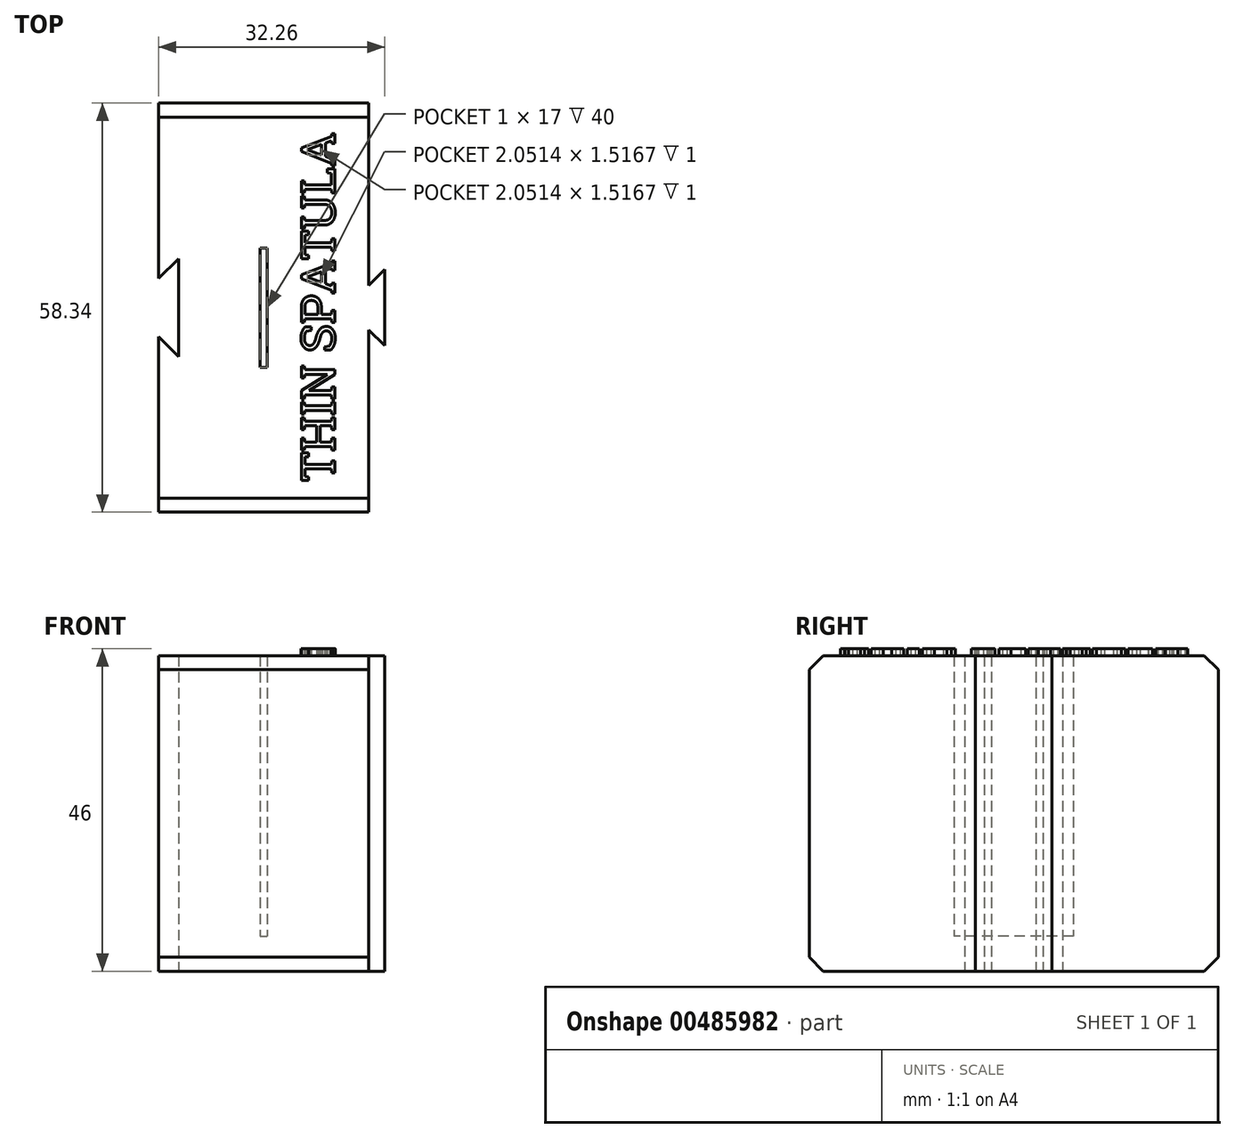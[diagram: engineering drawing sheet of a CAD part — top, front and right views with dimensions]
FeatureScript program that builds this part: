
annotation { "Feature Type Name" : "Feature", "Feature Type Description" : "" }
export const myFeature = defineFeature(function(context is Context, id is Id, definition is map)
    precondition{}
    {
        {
            var Q0;
            Q0=qCreatedBy(makeId("Top.planeOp"),FACE);
            var sketch = newSketch(context, id + "F0", { "sketchPlane" : qUnion([Q0])});
            skLineSegment(sketch, "E0", {"start": v(-15, 4.17) * mm, "end": v(-15, 29.17) * mm});
            skLineSegment(sketch, "E1", {"start": v(-15, 29.17) * mm, "end": v(15, 29.17) * mm});
            skLineSegment(sketch, "E2", {"start": v(15, 29.17) * mm, "end": v(15, 3.17) * mm});
            skLineSegment(sketch, "E3", {"start": v(-15, 4.17) * mm, "end": v(-12.17, 7) * mm});
            skLineSegment(sketch, "E4", {"start": v(-12.17, 7) * mm, "end": v(-12.17, 0) * mm});
            skLineSegment(sketch, "E5", {"start": v(15, 3.17) * mm, "end": v(17.26, 5.43) * mm});
            skLineSegment(sketch, "E6", {"start": v(17.26, 5.43) * mm, "end": v(17.26, -0.57) * mm});
            skLineSegment(sketch, "E7.MirrorCS", {"start": v(-15, -4.17) * mm, "end": v(-12.17, -7) * mm});
            skLineSegment(sketch, "E8.MirrorCS", {"start": v(15, -29.17) * mm, "end": v(15, -3.17) * mm});
            skLineSegment(sketch, "E9.MirrorCS", {"start": v(-12.17, -7) * mm, "end": v(-12.17, 0) * mm});
            skLineSegment(sketch, "E10.MirrorCS", {"start": v(-15, -4.17) * mm, "end": v(-15, -29.17) * mm});
            skLineSegment(sketch, "E11.MirrorCS", {"start": v(17.26, -5.43) * mm, "end": v(17.26, 0.57) * mm});
            skLineSegment(sketch, "E12.MirrorCS", {"start": v(15, -3.17) * mm, "end": v(17.26, -5.43) * mm});
            skLineSegment(sketch, "E13.MirrorCS", {"start": v(-15, -29.17) * mm, "end": v(15, -29.17) * mm});
            skLineSegment(sketch, "E14.bottom", {"start": v(-0.5, 8.5) * mm, "end": v(0.5, 8.5) * mm});
            skLineSegment(sketch, "E14.top", {"start": v(-0.5, -8.5) * mm, "end": v(0.5, -8.5) * mm});
            skLineSegment(sketch, "E14.left", {"start": v(-0.5, 8.5) * mm, "end": v(-0.5, -8.5) * mm});
            skLineSegment(sketch, "E14.right", {"start": v(0.5, 8.5) * mm, "end": v(0.5, -8.5) * mm});
            skPoint(sketch, "E14.middle", {"position": v(0, 0) * mm});
            skSolve(sketch);
        }
        {
            var Q0;
            Q0=qSketchRegion(id+"F0",true);
            extrude(context, id + "F1", {"entities" : qUnion([Q0]), "depth" : 40 * mm});
        }
        {
            var Q0;
            Q0=makeQuery(id+"F0.imprint","IMPRINT",FACE,{"disambiguationData":[TD([[makeQuery(id+"F0.imprint","IMPRINT",EDGE,{"derivedFrom":sQuery(id+"F0.wireOp",EDGE,"E0")}),-1.0]])]});
            var Q1;
            Q1=makeQuery(id+"F0.imprint","IMPRINT",FACE,{"disambiguationData":[TD([[makeQuery(id+"F0.imprint","IMPRINT",EDGE,{"derivedFrom":sQuery(id+"F0.wireOp",EDGE,"E14.bottom")}),-1.0]])]});
            extrude(context, id + "F2", {"entities" : qUnion([Q0, Q1]), "operationType" : NewBodyOperationType.ADD, "oppositeDirection" : true, "depth" : 5 * mm});
        }
        {
            var Q0;
            Q0=makeQuery(id+"F2.opExtrude","CAP_EDGE",EDGE,{"disambiguationData":[OSD([sQuery(id+"F0.wireOp",EDGE,"E13.MirrorCS")])],"isStart":false});
            var Q1;
            Q1=makeQuery(id+"F2.opExtrude","CAP_EDGE",EDGE,{"disambiguationData":[OSD([sQuery(id+"F0.wireOp",EDGE,"E1")])],"isStart":false});
            var Q2;
            Q2=makeQuery(id+"F1.opExtrude","CAP_EDGE",EDGE,{"disambiguationData":[OSD([sQuery(id+"F0.wireOp",EDGE,"E13.MirrorCS")])],"isStart":false});
            var Q3;
            Q3=makeQuery(id+"F1.opExtrude","CAP_EDGE",EDGE,{"disambiguationData":[OSD([sQuery(id+"F0.wireOp",EDGE,"E1")])],"isStart":false});
            chamfer(context, id + "F3", {"entities" : qUnion([Q0, Q1, Q2, Q3]), "width" : 2 * mm, "tangentPropagation" : true});
        }
        {
            var Q0;
            Q0=makeQuery(id+"F1.opExtrude","CAP_FACE",FACE,{"disambiguationData":[OSD([sQuery(id+"F0.wireOp",EDGE,"E0"),sQuery(id+"F0.wireOp",EDGE,"E1"),sQuery(id+"F0.wireOp",EDGE,"E2"),sQuery(id+"F0.wireOp",EDGE,"E3"),sQuery(id+"F0.wireOp",EDGE,"E4"),sQuery(id+"F0.wireOp",EDGE,"E5"),sQuery(id+"F0.wireOp",EDGE,"E6"),sQuery(id+"F0.wireOp",EDGE,"E7.MirrorCS"),sQuery(id+"F0.wireOp",EDGE,"E8.MirrorCS"),sQuery(id+"F0.wireOp",EDGE,"E9.MirrorCS"),sQuery(id+"F0.wireOp",EDGE,"E10.MirrorCS"),sQuery(id+"F0.wireOp",EDGE,"E11.MirrorCS"),sQuery(id+"F0.wireOp",EDGE,"E12.MirrorCS"),sQuery(id+"F0.wireOp",EDGE,"E13.MirrorCS"),sQuery(id+"F0.wireOp",EDGE,"E14.bottom"),sQuery(id+"F0.wireOp",EDGE,"E14.top"),sQuery(id+"F0.wireOp",EDGE,"E14.left"),sQuery(id+"F0.wireOp",EDGE,"E14.right")])],"isStart":false});
            var sketch = newSketch(context, id + "F4", { "sketchPlane" : qUnion([Q0])});
            skText(sketch, "E15", { "text": "THIN SPATULA", "fontName": "RobotoSlab-Regular.ttf"});
            const initialGuessF4  = {"E15": [0.01014, -0.0248, 0, 1, 0.00484]};
            skSetInitialGuess(sketch, initialGuessF4);
            skSolve(sketch);
        }
        {
            var Q0;
            Q0=qSketchRegion(id+"F4",true);
            extrude(context, id + "F5", {"entities" : qUnion([Q0]), "operationType" : NewBodyOperationType.ADD, "depth" : 1 * mm});
        }
    });
